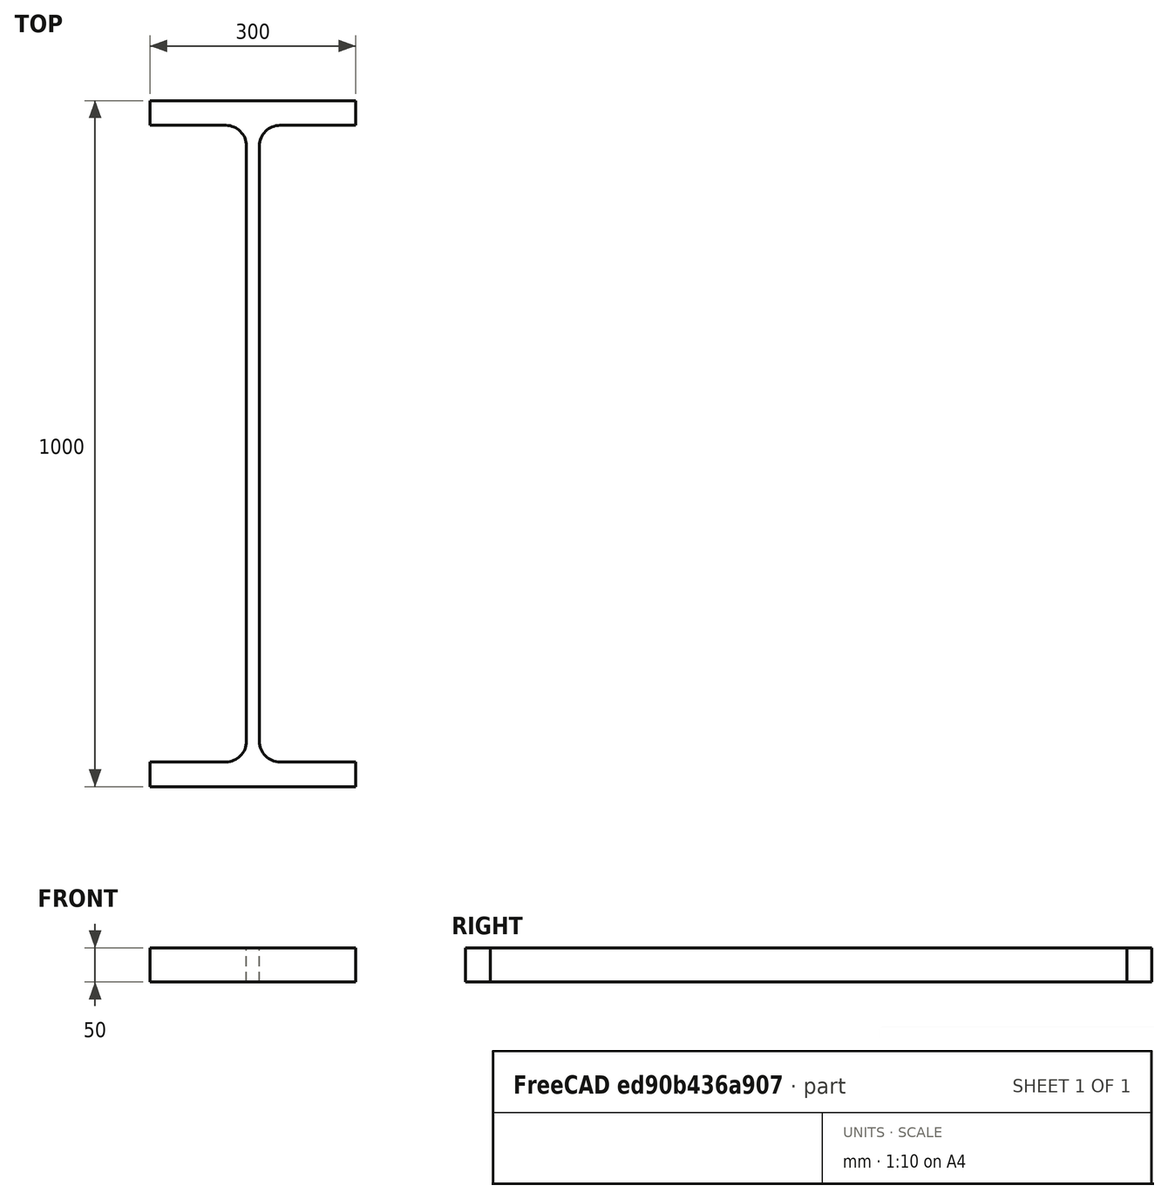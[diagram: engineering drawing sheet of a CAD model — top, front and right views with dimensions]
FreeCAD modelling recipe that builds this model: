
FCSTD DOCUMENT  (FreeCAD 0.15R4671 (Git))
Label: HE-B-Profile 1000 DIN1025-2 S235JR
License: All rights reserved
LicenseURL: http://en.wikipedia.org/wiki/All_rights_reserved
objects: Sketcher::SketchObject×1, Part::Extrusion×1
note: 2 computed .brp shape members not serialized (recipe doc carries the construction recipe); baked Part::Feature solids carry a one-line shape summary decoded from their .brp

FEATURE [Sketcher::SketchObject] Sketch
  sketch-geometry (16):
    g0: LineSegment StartX=9.5 StartY=-434 StartZ=0 EndX=9.5 EndY=434 EndZ=0
    g1: LineSegment StartX=39.5 StartY=464 StartZ=0 EndX=150 EndY=464 EndZ=0
    g2: LineSegment StartX=150 StartY=464 StartZ=0 EndX=150 EndY=500 EndZ=0
    g3: LineSegment StartX=150 StartY=500 StartZ=0 EndX=-150 EndY=500 EndZ=0
    g4: LineSegment StartX=-150 StartY=500 StartZ=0 EndX=-150 EndY=464 EndZ=0
    g5: LineSegment StartX=-150 StartY=464 StartZ=0 EndX=-39.5 EndY=464 EndZ=0
    g6: LineSegment StartX=-9.5 StartY=434 StartZ=0 EndX=-9.5 EndY=-434 EndZ=0
    g7: LineSegment StartX=-39.5 StartY=-464 StartZ=0 EndX=-150 EndY=-464 EndZ=0
    g8: LineSegment StartX=-150 StartY=-464 StartZ=0 EndX=-150 EndY=-500 EndZ=0
    g9: LineSegment StartX=-150 StartY=-500 StartZ=0 EndX=150 EndY=-500 EndZ=0
    g10: LineSegment StartX=150 StartY=-500 StartZ=0 EndX=150 EndY=-464 EndZ=0
    g11: LineSegment StartX=150 StartY=-464 StartZ=0 EndX=39.5 EndY=-464 EndZ=0
    g12: ArcOfCircle CenterX=39.5 CenterY=434 CenterZ=0 NormalX=0 NormalY=0 NormalZ=1 Radius=30 StartAngle=1.5708 EndAngle=3.14159
    g13: ArcOfCircle CenterX=39.5 CenterY=-434 CenterZ=0 NormalX=0 NormalY=0 NormalZ=1 Radius=30 StartAngle=3.14159 EndAngle=4.71239
    g14: ArcOfCircle CenterX=-39.5 CenterY=434 CenterZ=0 NormalX=0 NormalY=0 NormalZ=1 Radius=30 StartAngle=0 EndAngle=1.5708
    g15: ArcOfCircle CenterX=-39.5 CenterY=-434 CenterZ=0 NormalX=0 NormalY=0 NormalZ=1 Radius=30 StartAngle=4.71239 EndAngle=6.28319
  constraints (42):
    c: Vertical(g0)
    c: Coincident(g2,g1)
    c: Vertical(g2)
    c: Coincident(g3,g2)
    c: Coincident(g4,g3)
    c: Vertical(g4)
    c: Coincident(g5,g4)
    c: Horizontal(g5)
    c: Vertical(g6)
    c: Horizontal(g7)
    c: Coincident(g8,g7)
    c: Vertical(g8)
    c: Coincident(g9,g8)
    c: Horizontal(g9)
    c: Coincident(g10,g9)
    c: Vertical(g10)
    c: Coincident(g11,g10)
    c: Horizontal(g11)
    c: Tangent(g1,g12) = 1.5708
    c: Tangent(g0,g12) = 1.5708
    c: Tangent(g0,g13) = 1.5708
    c: Tangent(g11,g13) = 1.5708
    c: Tangent(g5,g14) = 1.5708
    c: Tangent(g6,g14) = 1.5708
    c: Tangent(g6,g15) = 1.5708
    c: Tangent(g7,g15) = 1.5708
    c: Equal(g3,g9)
    c: Equal(g2,g4)
    c: Equal(g4,g8)
    c: Equal(g8,g10)
    c: Equal(g12,g14)
    c: Equal(g14,g15)
    c: Equal(g15,g13)
    c: Symmetric(g2,g3,g-2)
    c: Symmetric(g9,g8,g-2)
    c: Symmetric(g0,g6,g-2)
    c: Symmetric(g2,g9,g-1)
    c: DistanceY(g2,g9) = -1000
    c: DistanceX(g3) = -300
    c: DistanceX(g0,g6) = -19
    c: DistanceY(g2) = 36
    c: Radius(g12) = 30
FEATURE [Part::Extrusion] Extrude  label="HE-B-Profile 1000 DIN1025-2 S235JR"
  Base = -> Sketch
  Dir = (0,0,50)
  Solid = true
